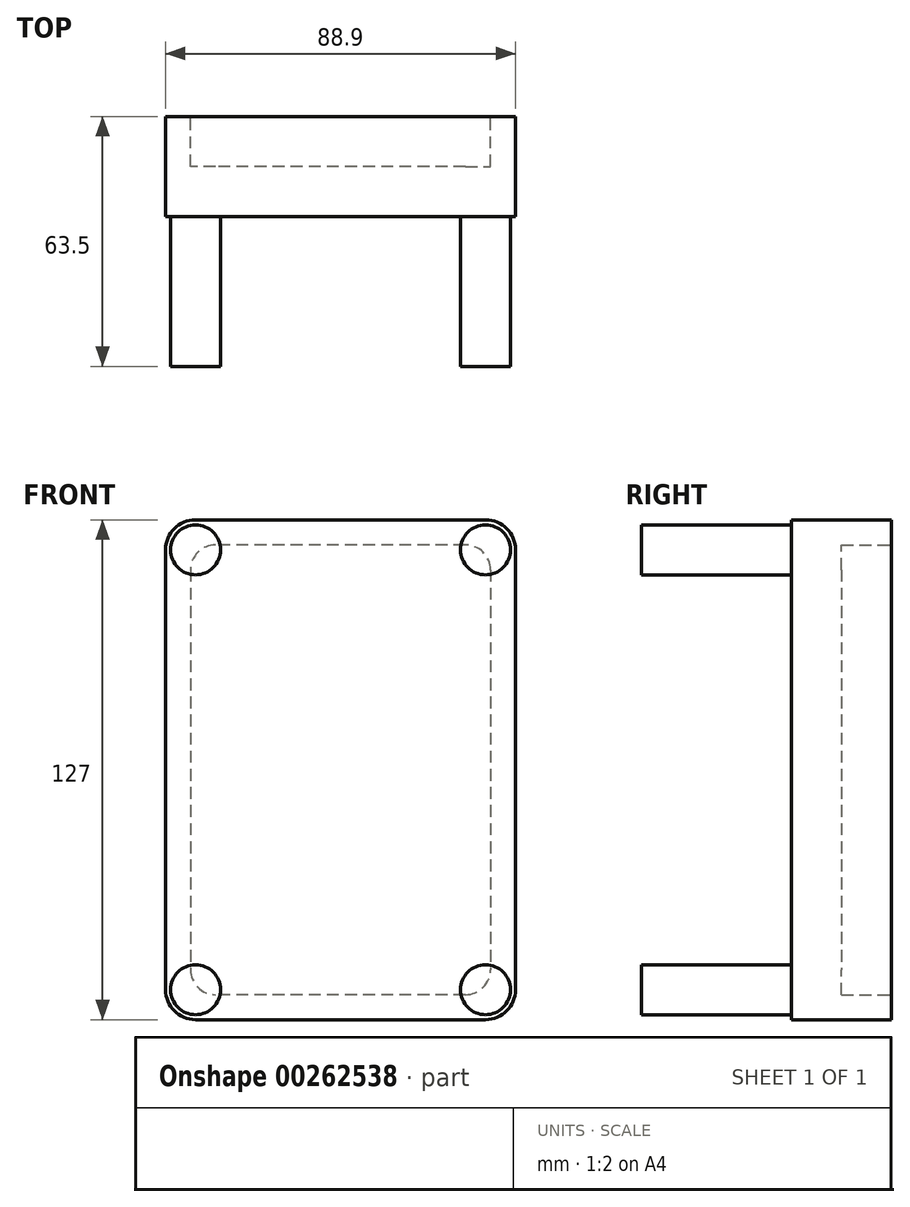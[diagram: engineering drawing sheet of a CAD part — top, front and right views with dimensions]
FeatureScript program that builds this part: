
annotation { "Feature Type Name" : "Feature", "Feature Type Description" : "" }
export const myFeature = defineFeature(function(context is Context, id is Id, definition is map)
    precondition{}
    {
        {
            var Q0;
            Q0=qCreatedBy(makeId("Front.planeOp"),FACE);
            var sketch = newSketch(context, id + "F0", { "sketchPlane" : qUnion([Q0])});
            skLineSegment(sketch, "E0.bottom", {"start": v(36.83, 63.5) * mm, "end": v(-36.83, 63.5) * mm});
            skLineSegment(sketch, "E0.top", {"start": v(36.83, -63.5) * mm, "end": v(-36.83, -63.5) * mm});
            skLineSegment(sketch, "E0.left", {"start": v(44.45, 55.88) * mm, "end": v(44.45, -55.88) * mm});
            skLineSegment(sketch, "E0.right", {"start": v(-44.45, 55.88) * mm, "end": v(-44.45, -55.88) * mm});
            skPoint(sketch, "E0.middle", {"position": v(0, 0) * mm});
            skLineSegment(sketch, "E1.bottom", {"start": v(31.75, 57.15) * mm, "end": v(-31.75, 57.15) * mm});
            skLineSegment(sketch, "E1.top", {"start": v(31.75, -57.15) * mm, "end": v(-31.75, -57.15) * mm});
            skLineSegment(sketch, "E1.left", {"start": v(38.1, 50.8) * mm, "end": v(38.1, -50.8) * mm});
            skLineSegment(sketch, "E1.right", {"start": v(-38.1, 50.8) * mm, "end": v(-38.1, -50.8) * mm});
            skPoint(sketch, "E2.visualSharp", {"position": v(-44.45, 63.5) * mm});
            skArc(sketch, "E2.filletArc", {"start": v(-36.83, 63.5) * mm, "mid": v(-42.22, 61.27) * mm, "end": v(-44.45, 55.88) * mm});
            skPoint(sketch, "E3.visualSharp", {"position": v(44.45, 63.5) * mm});
            skArc(sketch, "E3.filletArc", {"start": v(44.45, 55.88) * mm, "mid": v(42.22, 61.27) * mm, "end": v(36.83, 63.5) * mm});
            skPoint(sketch, "E4.visualSharp", {"position": v(-44.45, -63.5) * mm});
            skArc(sketch, "E4.filletArc", {"start": v(-44.45, -55.88) * mm, "mid": v(-42.22, -61.27) * mm, "end": v(-36.83, -63.5) * mm});
            skPoint(sketch, "E5.visualSharp", {"position": v(44.45, -63.5) * mm});
            skArc(sketch, "E5.filletArc", {"start": v(36.83, -63.5) * mm, "mid": v(42.22, -61.27) * mm, "end": v(44.45, -55.88) * mm});
            skPoint(sketch, "E6.visualSharp", {"position": v(38.1, 57.15) * mm});
            skArc(sketch, "E6.filletArc", {"start": v(38.1, 50.8) * mm, "mid": v(36.24, 55.3) * mm, "end": v(31.75, 57.15) * mm});
            skPoint(sketch, "E7.visualSharp", {"position": v(38.1, -57.15) * mm});
            skArc(sketch, "E7.filletArc", {"start": v(31.75, -57.15) * mm, "mid": v(36.24, -55.3) * mm, "end": v(38.1, -50.8) * mm});
            skPoint(sketch, "E8.visualSharp", {"position": v(-38.1, -57.15) * mm});
            skArc(sketch, "E8.filletArc", {"start": v(-38.1, -50.8) * mm, "mid": v(-36.24, -55.3) * mm, "end": v(-31.75, -57.15) * mm});
            skPoint(sketch, "E9.visualSharp", {"position": v(-38.1, 57.15) * mm});
            skArc(sketch, "E9.filletArc", {"start": v(-31.75, 57.15) * mm, "mid": v(-36.24, 55.3) * mm, "end": v(-38.1, 50.8) * mm});
            skSolve(sketch);
        }
        {
            var Q0;
            Q0=makeQuery(id+"F0.imprint","IMPRINT",FACE,{"disambiguationData":[TD([[makeQuery(id+"F0.imprint","IMPRINT",EDGE,{"derivedFrom":sQuery(id+"F0.wireOp",EDGE,"E0.bottom")}),1.0]])]});
            var Q1;
            Q1=makeQuery(id+"F0.imprint","IMPRINT",FACE,{"disambiguationData":[TD([[makeQuery(id+"F0.imprint","IMPRINT",EDGE,{"derivedFrom":sQuery(id+"F0.wireOp",EDGE,"E1.bottom")}),1.0]])]});
            extrude(context, id + "F1", {"entities" : qUnion([Q0, Q1]), "depth" : 25.4 * mm});
        }
        {
            var Q0;
            Q0=makeQuery(id+"F0.imprint","IMPRINT",FACE,{"disambiguationData":[TD([[makeQuery(id+"F0.imprint","IMPRINT",EDGE,{"derivedFrom":sQuery(id+"F0.wireOp",EDGE,"E1.bottom")}),1.0]])]});
            extrude(context, id + "F2", {"entities" : qUnion([Q0]), "operationType" : NewBodyOperationType.REMOVE, "depth" : 12.7 * mm});
        }
        {
            var Q0;
            Q0=makeQuery(id+"F1.opExtrude","CAP_FACE",FACE,{"disambiguationData":[OSD([sQuery(id+"F0.wireOp",EDGE,"E0.bottom"),sQuery(id+"F0.wireOp",EDGE,"E0.top"),sQuery(id+"F0.wireOp",EDGE,"E0.left"),sQuery(id+"F0.wireOp",EDGE,"E0.right"),sQuery(id+"F0.wireOp",EDGE,"E2.filletArc"),sQuery(id+"F0.wireOp",EDGE,"E3.filletArc"),sQuery(id+"F0.wireOp",EDGE,"E4.filletArc"),sQuery(id+"F0.wireOp",EDGE,"E5.filletArc")])],"isStart":false});
            var sketch = newSketch(context, id + "F3", { "sketchPlane" : qUnion([Q0])});
            skCircle(sketch, "E10", {"center": v(-36.83, 55.88) * mm, "radius": 6.35 * mm});
            skCircle(sketch, "E11", {"center": v(36.83, 55.88) * mm, "radius": 6.35 * mm});
            skCircle(sketch, "E12", {"center": v(-36.83, -55.88) * mm, "radius": 6.35 * mm});
            skCircle(sketch, "E13", {"center": v(36.83, -55.88) * mm, "radius": 6.35 * mm});
            skSolve(sketch);
        }
        {
            var Q0;
            Q0 = qSketchRegion(id + "F3", true);
            extrude(context, id + "F4", {"entities" : qUnion([Q0]), "operationType" : NewBodyOperationType.ADD, "depth" : 38.1 * mm});
        }
    });
